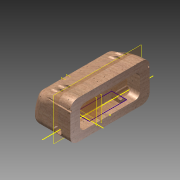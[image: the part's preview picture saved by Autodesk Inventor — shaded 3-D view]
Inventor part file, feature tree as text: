
AUTODESK INVENTOR PART (.ipt)
format: ipt  version: 2015 (Build 190159000, 159)  size: 291,328 bytes
history: native  units: in
note: dims shown in document units (in); Inventor stores cm internally (conversion verified against a paired STEP export)
features: extrude x7, sketch x5, fillet x4, plane x4, hole x2
ambient origin geometry x8: Origin, YZ Plane, XZ Plane, XY Plane, X Axis, Y Axis, Z Axis, Center Point
bodies: Solid1 (feature_tree)
feature tree (22):
  sketch  "Sketch1"  dims[d0=3.17in d1=1.53in d2=1.6in d3=0.0in]
  extrude  "Extrusion1"  Depth=1.53in
  fillet  "Fillet3"  Radius=1.6in
  sketch  "Sketch5"  dims[d20=1.1in d22=1.4in d25=1.15in d26=1.25in]
  extrude  "Extrusion5"  Depth=1.4in
  fillet  "Fillet4"  Radius=1.15in
  fillet  "Fillet5"  Radius=1.25in
  extrude  "Extrusion6"  Depth=0.09in
  fillet  "Fillet6"  Radius=0.13in
  plane  "Work Plane1"
  hole  "Hole1"  [1 undecoded]
  extrude  "Extrusion8"  Depth=0.3in
  hole  "Hole2"  [1 undecoded]
  plane  "Work Plane2"
  plane  "Work Plane3"
  sketch  "Sketch9"  dims[d34=0.2in d35=0.3in d36=1.0in d37=0.0in d39=2.4in d40=0.93in d42=0.0in d43=0.57in d45=0.2in d46=0.27in d47=2.0in d48=1.35in d49=0.2in d50=0.75in d51=0.375in d52=0.25in d53=0.5635in d54=1.0in d55=0.8108in d56=0.3in d57=0.06in d58=1.0in d59=0.0in d60=0.3in d61=0.5in d62=0.29in d63=0.75in d64=0.375in d65=0.25in d66=0.5635in d67=0.35in d68=0.8108in d70=-0.5in d71=-1.0in d72=1.45in d73=0.05in d74=0.3in d75=0.3in d76=0.27in d77=0.0in d78=0.27in d79=0.0in d80=-0.2in]
  extrude  "Extrusion9"  Depth=2.4in TaperAngle=0.0deg
  extrude  "Extrusion10"  Depth=0.2in
  plane  "Work Plane4"
  sketch  "Sketch7"  dims[d30=1.0in d31=0.0in d33=0.3in]
  sketch  "Sketch6"  dims[d27=0.2in d28=0.09in d29=0.13in]
  extrude  "Extrusion7"  Depth=0.27in
note: 2 required parameter values undecoded (feature->parameter linkage not recoverable at this tier; creation-order binding heuristic only, values carry confidence <= 0.55)
